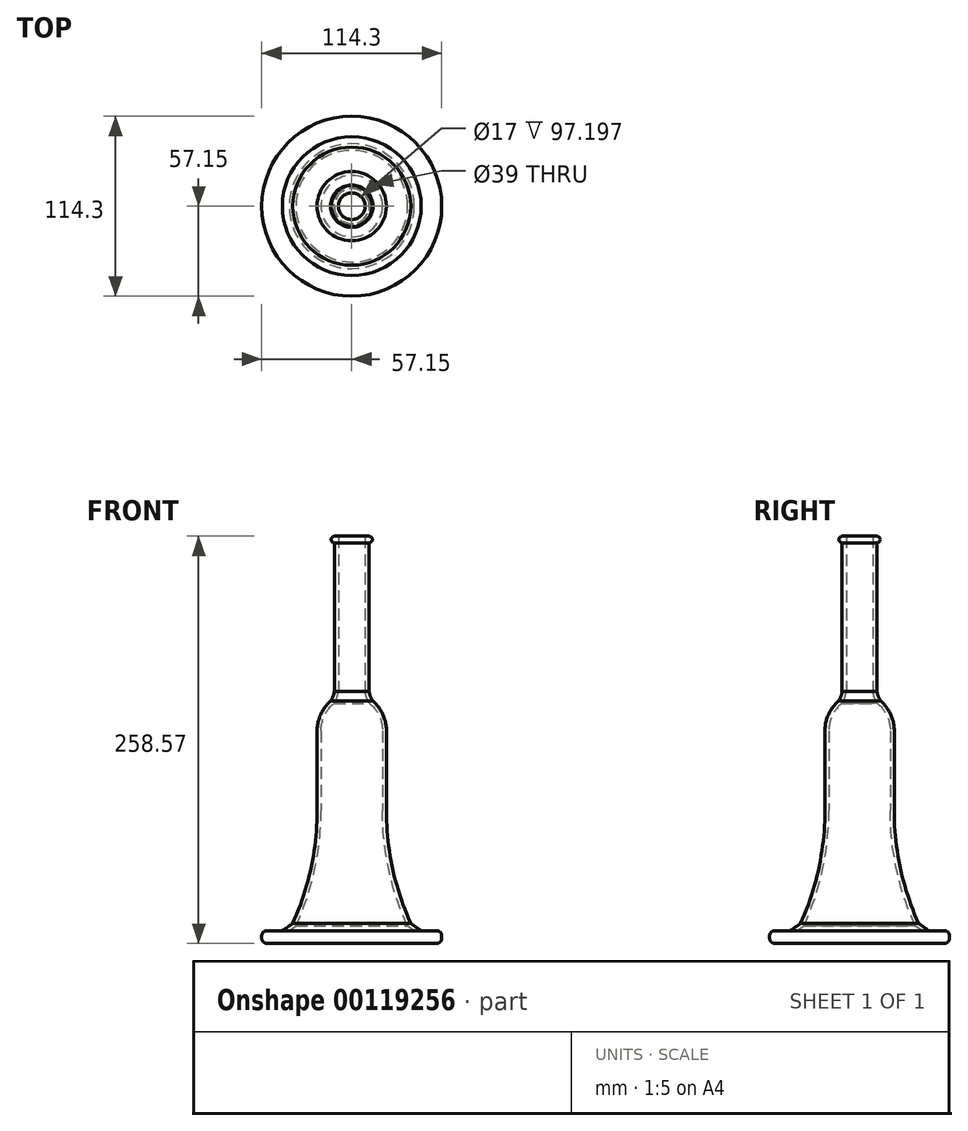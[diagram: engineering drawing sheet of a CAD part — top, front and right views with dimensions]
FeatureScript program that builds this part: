
annotation { "Feature Type Name" : "Feature", "Feature Type Description" : "" }
export const myFeature = defineFeature(function(context is Context, id is Id, definition is map)
    precondition{}
    {
        {
            var Q0;
            Q0=qCreatedBy(makeId("Front.planeOp"),FACE);
            var sketch = newSketch(context, id + "F0", { "sketchPlane" : qUnion([Q0])});
            skLineSegment(sketch, "E0", {"start": v(0, 0) * mm, "end": v(0, 8) * mm});
            skLineSegment(sketch, "E1", {"start": v(0, 8) * mm, "end": v(37.5, 8) * mm});
            skLineSegment(sketch, "E2", {"start": v(37.5, 8) * mm, "end": v(37.5, 0) * mm});
            skLineSegment(sketch, "E3", {"start": v(22, 84.2) * mm, "end": v(22, 135) * mm});
            skArc(sketch, "E4", {"start": v(22, 84.2) * mm, "mid": v(25.92, 47.58) * mm, "end": v(37.5, 12.62) * mm});
            skPoint(sketch, "E5.visualSharp", {"position": v(11, 156.97) * mm});
            skArc(sketch, "E5.filletArc", {"start": v(11.09, 159.9) * mm, "mid": v(11.88, 156.74) * mm, "end": v(13.44, 153.89) * mm});
            skLineSegment(sketch, "E6", {"start": v(37.5, 8) * mm, "end": v(50.68, 8) * mm});
            skArc(sketch, "E7", {"start": v(37.5, 12.62) * mm, "mid": v(40.77, 10.27) * mm, "end": v(44.1, 8) * mm});
            skArc(sketch, "E8.1", {"start": v(8.5, 161.38) * mm, "mid": v(9.25, 156.66) * mm, "end": v(11.43, 152.41) * mm});
            skArc(sketch, "E8.2", {"start": v(35.5, 11) * mm, "mid": v(39.07, 8.41) * mm, "end": v(42.7, 5.92) * mm});
            skArc(sketch, "E8.3", {"start": v(19.5, 84.2) * mm, "mid": v(23.55, 46.73) * mm, "end": v(35.5, 11) * mm});
            skLineSegment(sketch, "E8.4", {"start": v(19.5, 84.2) * mm, "end": v(19.5, 135) * mm});
            skLineSegment(sketch, "E9", {"start": v(8.5, 258.57) * mm, "end": v(11, 258.57) * mm});
            skArc(sketch, "E10", {"start": v(22, 135) * mm, "mid": v(19.76, 145.37) * mm, "end": v(13.44, 153.89) * mm});
            skArc(sketch, "E11", {"start": v(19.5, 135) * mm, "mid": v(17.38, 144.6) * mm, "end": v(11.43, 152.41) * mm});
            skLineSegment(sketch, "E12", {"start": v(8.5, 258.57) * mm, "end": v(8.5, 161.38) * mm});
            skLineSegment(sketch, "E13", {"start": v(11.09, 159.9) * mm, "end": v(11.09, 254.4) * mm});
            skArc(sketch, "E14", {"start": v(11, 258.57) * mm, "mid": v(13.09, 256.53) * mm, "end": v(11.09, 254.4) * mm});
            skSolve(sketch);
        }
        {
            var Q0;
            Q0=qCreatedBy(makeId("Front.planeOp"),FACE);
            var sketch = newSketch(context, id + "F1", { "sketchPlane" : qUnion([Q0])});
            skLineSegment(sketch, "E15", {"start": v(0, 0) * mm, "end": v(53.93, 0) * mm});
            skLineSegment(sketch, "E16", {"start": v(57.15, 3.22) * mm, "end": v(57.15, 4.78) * mm});
            skLineSegment(sketch, "E17", {"start": v(53.93, 8) * mm, "end": v(0, 8) * mm});
            skLineSegment(sketch, "E18", {"start": v(0, 8) * mm, "end": v(0, 0) * mm});
            skPoint(sketch, "E19.visualSharp", {"position": v(57.15, 8) * mm});
            skArc(sketch, "E19.filletArc", {"start": v(57.15, 4.78) * mm, "mid": v(56.2, 7.06) * mm, "end": v(53.93, 8) * mm});
            skPoint(sketch, "E20.visualSharp", {"position": v(57.15, 0) * mm});
            skArc(sketch, "E20.filletArc", {"start": v(53.93, 0) * mm, "mid": v(56.2, 0.94) * mm, "end": v(57.15, 3.22) * mm});
            skSolve(sketch);
        }
        {
            var Q0;
            Q0=makeQuery(id+"F1.imprint","IMPRINT",FACE,{"disambiguationData":[TD([[makeQuery(id+"F1.imprint","IMPRINT",EDGE,{"derivedFrom":sQuery(id+"F1.wireOp",EDGE,"E15")}),1.0]])]});
            var Q1;
            Q1=sQuery(id+"F1.wireOp",EDGE,"E18");
            revolve(context, id + "F2", {"entities" : qUnion([Q0]), "axis" : qUnion([Q1]), "revolveType" : RevolveType.FULL});
        }
        {
            var Q0;
            Q0=makeQuery(id+"F0.imprint","IMPRINT",FACE,{"disambiguationData":[TD([[makeQuery(id+"F0.imprint","IMPRINT",EDGE,{"derivedFrom":sQuery(id+"F0.wireOp",EDGE,"E3")}),1.0]])]});
            var Q1;
            Q1=sQuery(id+"F0.wireOp",EDGE,"E0");
            revolve(context, id + "F3", {"operationType" : NewBodyOperationType.ADD, "entities" : qUnion([Q0]), "axis" : qUnion([Q1]), "revolveType" : RevolveType.FULL});
        }
    });
